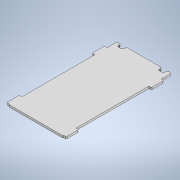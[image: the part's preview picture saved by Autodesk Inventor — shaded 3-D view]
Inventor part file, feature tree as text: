
AUTODESK INVENTOR PART (.ipt)
format: ipt  version: 2020 (Build 240168000, 168)  size: 187,904 bytes
history: native  units: mm
features: extrude x1, sketch x1
ambient origin geometry x8: Origin, YZ Plane, XZ Plane, XY Plane, X Axis, Y Axis, Z Axis, Center Point
bodies: Solid1 (feature_tree)
feature tree (2):
  extrude  "Extrusion1"  Depth=2.0mm
  sketch  "Sketch1"  dims[d3=6.0mm d8=2.0mm d11=2.0mm d12=2.0mm d13=9.0mm d14=83.0mm d15=12.7mm d16=12.7mm d17=2.0mm d18=3.0mm d19=3.0mm d24=6.0mm d25=1.0mm d26=1.0mm d27=5.0mm d28=0.0mm d29=29.0mm d30=23.325mm d31=2.0mm d34=2.0mm d35=126.5mm d36=244.0mm d37=29.0mm d38=1.67505mm]
